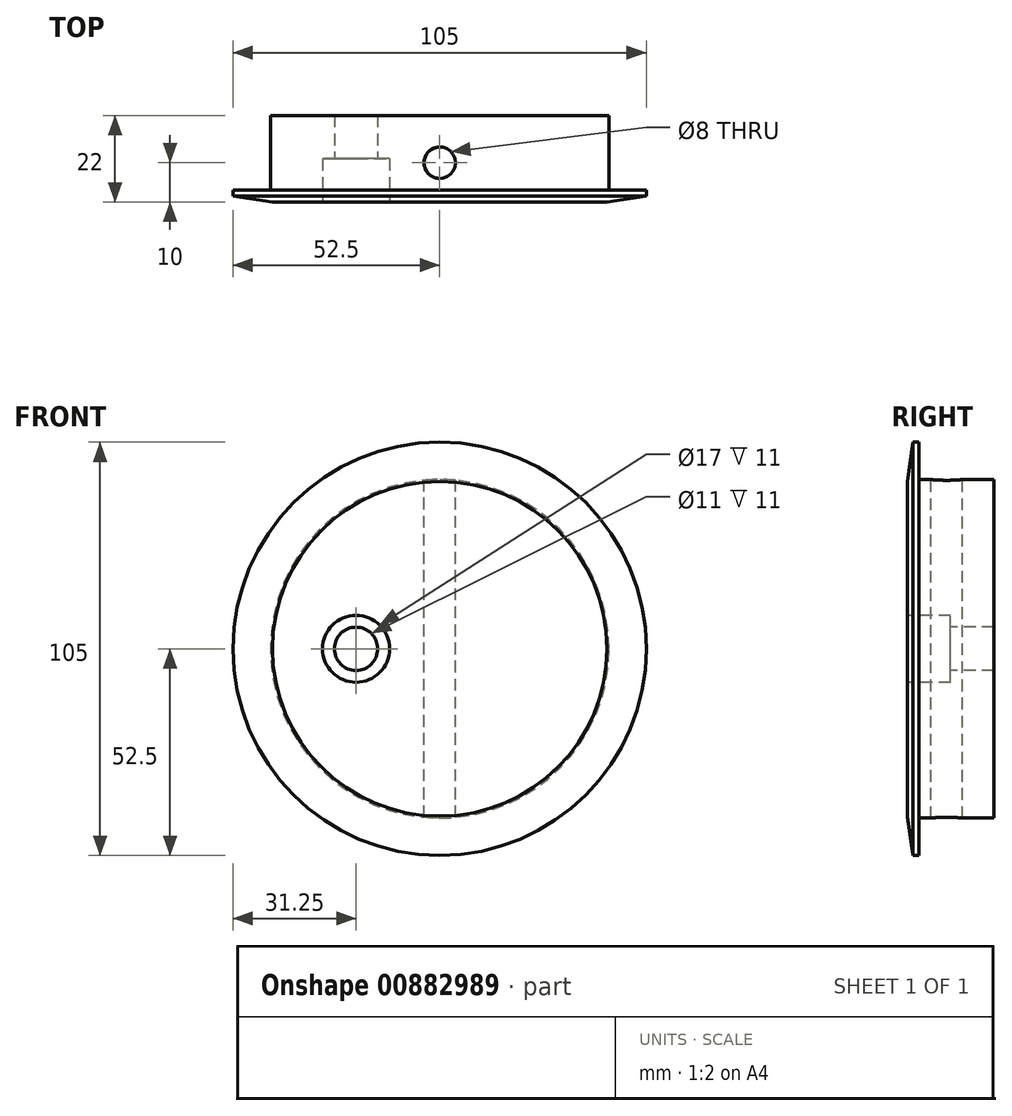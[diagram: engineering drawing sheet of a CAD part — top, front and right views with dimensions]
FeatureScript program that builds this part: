
annotation { "Feature Type Name" : "Feature", "Feature Type Description" : "" }
export const myFeature = defineFeature(function(context is Context, id is Id, definition is map)
    precondition{}
    {
        {
            var Q0;
            Q0=qCreatedBy(makeId("Front.planeOp"),FACE);
            var sketch = newSketch(context, id + "F0", { "sketchPlane" : qUnion([Q0])});
            skCircle(sketch, "E0", {"center": v(0, 0) * mm, "radius": 52.5 * mm});
            skSolve(sketch);
        }
        {
            var Q0;
            Q0 = qSketchRegion(id + "F0", true);
            extrude(context, id + "F1", {"entities" : qUnion([Q0]), "depth" : 3 * mm, "offsetDistance" : 25 * mm});
        }
        {
            var Q0;
            Q0=makeQuery(id+"F1.opExtrude","CAP_FACE",FACE,{"disambiguationData":[OSD([sQuery(id+"F0.wireOp",EDGE,"E0")])],"isStart":false});
            var sketch = newSketch(context, id + "F2", { "sketchPlane" : qUnion([Q0])});
            skCircle(sketch, "E1", {"center": v(0, 0) * mm, "radius": 43 * mm});
            skSolve(sketch);
        }
        {
            var Q0;
            Q0 = qSketchRegion(id + "F2", true);
            extrude(context, id + "F3", {"entities" : qUnion([Q0]), "operationType" : NewBodyOperationType.ADD, "oppositeDirection" : true, "depth" : 22 * mm, "offsetDistance" : 25 * mm});
        }
        {
            var Q0;
            Q0=makeQuery(id+"F1.opExtrude","CAP_FACE",FACE,{"disambiguationData":[OSD([sQuery(id+"F0.wireOp",EDGE,"E0")])],"isStart":false});
            var sketch = newSketch(context, id + "F4", { "sketchPlane" : qUnion([Q0])});
            skCircle(sketch, "E2", {"center": v(0, 0) * mm, "radius": 39 * mm});
            skLineSegment(sketch, "E3", {"start": v(-39, 0) * mm, "end": v(-21.25, 0) * mm, "construction": true});
            skCircle(sketch, "E4", {"center": v(-21.25, 0) * mm, "radius": 8.5 * mm});
            skSolve(sketch);
        }
        {
            var Q0;
            Q0=makeQuery(id+"F4.imprint","IMPRINT",FACE,{"disambiguationData":[TD([[makeQuery(id+"F4.imprint","IMPRINT",EDGE,{"derivedFrom":sQuery(id+"F4.wireOp",EDGE,"E4")}),1.0]])]});
            extrude(context, id + "F5", {"entities" : qUnion([Q0]), "operationType" : NewBodyOperationType.REMOVE, "oppositeDirection" : true, "depth" : 11 * mm, "offsetDistance" : 25 * mm});
        }
        {
            var Q0;
            Q0=makeQuery(id+"F5.boolean.opBoolean","COPY",FACE,{"derivedFrom":makeQuery(id+"F5.opExtrude","CAP_FACE",FACE,{"disambiguationData":[OSD([sQuery(id+"F4.wireOp",EDGE,"E4")])],"isStart":false})});
            var sketch = newSketch(context, id + "F6", { "sketchPlane" : qUnion([Q0])});
            skCircle(sketch, "E5", {"center": v(-21.25, 0) * mm, "radius": 5.5 * mm});
            skSolve(sketch);
        }
        {
            var Q0;
            Q0 = qSketchRegion(id + "F6", true);
            extrude(context, id + "F7", {"entities" : qUnion([Q0]), "operationType" : NewBodyOperationType.REMOVE, "endBound" : BoundingType.THROUGH_ALL, "oppositeDirection" : true, "depth" : 25 * mm, "offsetDistance" : 25 * mm});
        }
        {
            var Q0;
            Q0=makeQuery(id+"F1.opExtrude","CAP_EDGE",EDGE,{"disambiguationData":[OSD([sQuery(id+"F0.wireOp",EDGE,"E0")])],"isStart":false});
            chamfer(context, id + "F8", {"entities" : qUnion([Q0]), "chamferType" : ChamferType.TWO_OFFSETS, "width1" : 10 * mm, "oppositeDirection" : false, "width2" : 1.5 * mm, "tangentPropagation" : true});
        }
        {
            var Q0;
            Q0=qCreatedBy(makeId("Top.planeOp"),FACE);
            var sketch = newSketch(context, id + "F9", { "sketchPlane" : qUnion([Q0])});
            skLineSegment(sketch, "E6", {"start": v(0, 0) * mm, "end": v(0, 7) * mm, "construction": true});
            skLineSegment(sketch, "E7", {"start": v(0, 7) * mm, "end": v(0, 7) * mm});
            skCircle(sketch, "E8", {"center": v(0, 7) * mm, "radius": 4 * mm});
            skSolve(sketch);
        }
        {
            var Q0;
            Q0=makeQuery(id+"F9.imprint","IMPRINT",FACE,{"disambiguationData":[TD([[makeQuery(id+"F9.imprint","IMPRINT",EDGE,{"derivedFrom":sQuery(id+"F9.wireOp",EDGE,"E8")}),1.0]])]});
            var Q1;
            Q1=sQuery(id+"F9.wireOp",EDGE,"E8");
            extrude(context, id + "F10", {"entities" : qUnion([Q0]), "operationType" : NewBodyOperationType.REMOVE, "surfaceEntities" : qUnion([Q1]), "endBound" : BoundingType.SYMMETRIC, "oppositeDirection" : true, "depth" : 100 * mm, "offsetDistance" : 25 * mm});
        }
    });
